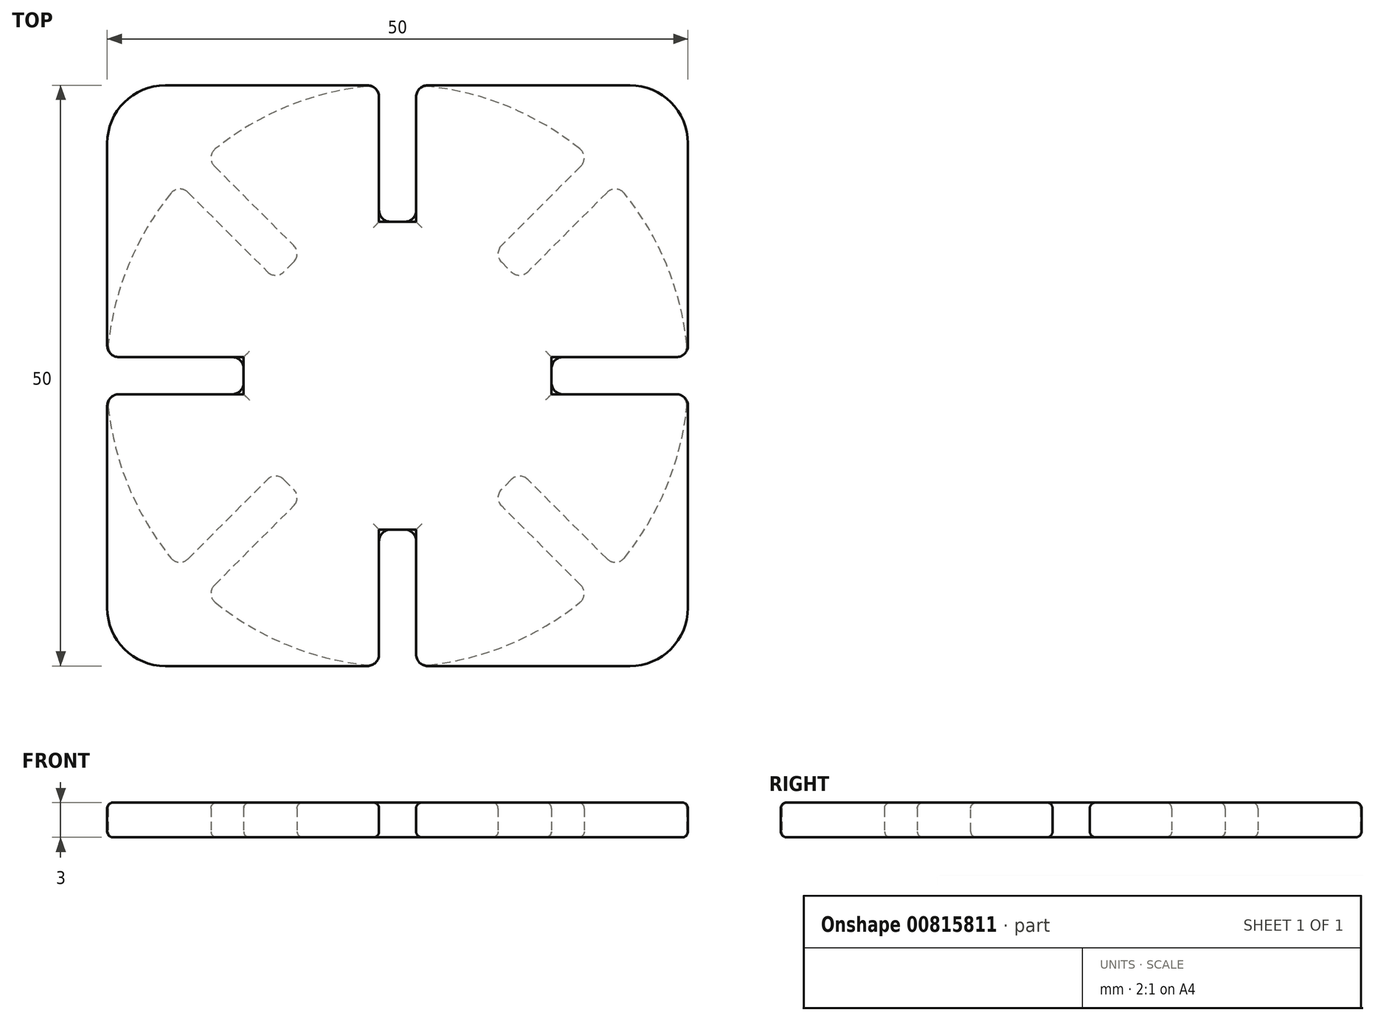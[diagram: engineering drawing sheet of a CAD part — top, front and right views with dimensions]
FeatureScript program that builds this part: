
annotation { "Feature Type Name" : "Feature", "Feature Type Description" : "" }
export const myFeature = defineFeature(function(context is Context, id is Id, definition is map)
    precondition{}
    {
        {
            assignVariable(context, id + "F0", {"name" : "thickness", "anyValue" : 3 * mm});
        }
        {
            var Q0;
            Q0=qCreatedBy(makeId("Top.planeOp"),FACE);
            var sketch = newSketch(context, id + "F1", { "sketchPlane" : qUnion([Q0])});
            skLineSegment(sketch, "E0.bottom", {"start": v(25, -25) * mm, "end": v(-25, -25) * mm});
            skLineSegment(sketch, "E0.top", {"start": v(25, 25) * mm, "end": v(-25, 25) * mm});
            skLineSegment(sketch, "E0.left", {"start": v(25, -25) * mm, "end": v(25, 25) * mm});
            skLineSegment(sketch, "E0.right", {"start": v(-25, -25) * mm, "end": v(-25, 25) * mm});
            skPoint(sketch, "E0.middle", {"position": v(0, 0) * mm});
            skLineSegment(sketch, "E1.bottom", {"start": v(25, 1.6) * mm, "end": v(13.25, 1.6) * mm});
            skLineSegment(sketch, "E1.top", {"start": v(25, -1.6) * mm, "end": v(13.25, -1.6) * mm});
            skLineSegment(sketch, "E1.left", {"start": v(25, 1.6) * mm, "end": v(25, -1.6) * mm});
            skLineSegment(sketch, "E1.right", {"start": v(13.25, 1.6) * mm, "end": v(13.25, -1.6) * mm});
            skLineSegment(sketch, "E2.bottom", {"start": v(-25, 1.6) * mm, "end": v(-13.25, 1.6) * mm});
            skLineSegment(sketch, "E2.top", {"start": v(-25, -1.6) * mm, "end": v(-13.25, -1.6) * mm});
            skLineSegment(sketch, "E2.left", {"start": v(-25, 1.6) * mm, "end": v(-25, -1.6) * mm});
            skLineSegment(sketch, "E2.right", {"start": v(-13.25, 1.6) * mm, "end": v(-13.25, -1.6) * mm});
            skLineSegment(sketch, "E3.bottom", {"start": v(-1.6, 25) * mm, "end": v(1.6, 25) * mm});
            skLineSegment(sketch, "E3.top", {"start": v(-1.6, 13.25) * mm, "end": v(1.6, 13.25) * mm});
            skLineSegment(sketch, "E3.left", {"start": v(-1.6, 25) * mm, "end": v(-1.6, 13.25) * mm});
            skLineSegment(sketch, "E3.right", {"start": v(1.6, 25) * mm, "end": v(1.6, 13.25) * mm});
            skLineSegment(sketch, "E4.bottom", {"start": v(-1.6, -25) * mm, "end": v(1.6, -25) * mm});
            skLineSegment(sketch, "E4.top", {"start": v(-1.6, -13.25) * mm, "end": v(1.6, -13.25) * mm});
            skLineSegment(sketch, "E4.left", {"start": v(-1.6, -25) * mm, "end": v(-1.6, -13.25) * mm});
            skLineSegment(sketch, "E4.right", {"start": v(1.6, -25) * mm, "end": v(1.6, -13.25) * mm});
            skSolve(sketch);
        }
        {
            var Q0;
            {var subQ1=sQuery(id+"F1.wireOp",EDGE,"E1.bottom");Q0=makeQuery(id+"F1.imprint","IMPRINT",FACE,{"disambiguationData":[TD([[makeQuery(id+"F1.imprint","IMPRINT",EDGE,{"derivedFrom":subQ1}),-1.0]])]});}
            extrude(context, id + "F2", {"entities" : qUnion([Q0]), "depth" : getVariable(context, 'thickness'), "offsetDistance" : 25 * mm});
        }
        {
            var Q0;
            Q0=makeQuery(id+"F2.opExtrude","SWEPT_EDGE",EDGE,{"disambiguationData":[OSD([sQuery(id+"F1.wireOp",EDGE,"E0.bottom"),sQuery(id+"F1.wireOp",EDGE,"E0.left")])]});
            var Q1;
            Q1=makeQuery(id+"F2.opExtrude","SWEPT_EDGE",EDGE,{"disambiguationData":[OSD([sQuery(id+"F1.wireOp",EDGE,"E0.bottom"),sQuery(id+"F1.wireOp",EDGE,"E0.right")])]});
            var Q2;
            Q2=makeQuery(id+"F2.opExtrude","SWEPT_EDGE",EDGE,{"disambiguationData":[OSD([sQuery(id+"F1.wireOp",EDGE,"E0.top"),sQuery(id+"F1.wireOp",EDGE,"E0.left")])]});
            var Q3;
            Q3=makeQuery(id+"F2.opExtrude","SWEPT_EDGE",EDGE,{"disambiguationData":[OSD([sQuery(id+"F1.wireOp",EDGE,"E0.top"),sQuery(id+"F1.wireOp",EDGE,"E0.right")])]});
            fillet(context, id + "F3", {"entities" : qUnion([Q0, Q1, Q2, Q3]), "radius" : 5 * mm, "tangentPropagation" : true, "allowEdgeOverflow" : false});
        }
        {
            var Q0;
            Q0=makeQuery(id+"F2.opExtrude","SWEPT_EDGE",EDGE,{"disambiguationData":[OSD([sQuery(id+"F1.wireOp",EDGE,"E0.bottom"),sQuery(id+"F1.wireOp",EDGE,"E4.bottom"),sQuery(id+"F1.wireOp",EDGE,"E4.left")])]});
            var Q1;
            Q1=makeQuery(id+"F2.opExtrude","SWEPT_EDGE",EDGE,{"disambiguationData":[OSD([sQuery(id+"F1.wireOp",EDGE,"E0.bottom"),sQuery(id+"F1.wireOp",EDGE,"E4.bottom"),sQuery(id+"F1.wireOp",EDGE,"E4.right")])]});
            var Q2;
            Q2=makeQuery(id+"F2.opExtrude","SWEPT_EDGE",EDGE,{"disambiguationData":[OSD([sQuery(id+"F1.wireOp",EDGE,"E0.left"),sQuery(id+"F1.wireOp",EDGE,"E1.top"),sQuery(id+"F1.wireOp",EDGE,"E1.left")])]});
            var Q3;
            Q3=makeQuery(id+"F2.opExtrude","SWEPT_EDGE",EDGE,{"disambiguationData":[OSD([sQuery(id+"F1.wireOp",EDGE,"E0.left"),sQuery(id+"F1.wireOp",EDGE,"E1.bottom"),sQuery(id+"F1.wireOp",EDGE,"E1.left")])]});
            var Q4;
            Q4=makeQuery(id+"F2.opExtrude","SWEPT_EDGE",EDGE,{"disambiguationData":[OSD([sQuery(id+"F1.wireOp",EDGE,"E0.right"),sQuery(id+"F1.wireOp",EDGE,"E2.bottom"),sQuery(id+"F1.wireOp",EDGE,"E2.left")])]});
            var Q5;
            Q5=makeQuery(id+"F2.opExtrude","SWEPT_EDGE",EDGE,{"disambiguationData":[OSD([sQuery(id+"F1.wireOp",EDGE,"E0.top"),sQuery(id+"F1.wireOp",EDGE,"E3.bottom"),sQuery(id+"F1.wireOp",EDGE,"E3.left")])]});
            var Q6;
            Q6=makeQuery(id+"F2.opExtrude","SWEPT_EDGE",EDGE,{"disambiguationData":[OSD([sQuery(id+"F1.wireOp",EDGE,"E0.top"),sQuery(id+"F1.wireOp",EDGE,"E3.bottom"),sQuery(id+"F1.wireOp",EDGE,"E3.right")])]});
            var Q7;
            Q7=makeQuery(id+"F2.opExtrude","SWEPT_EDGE",EDGE,{"disambiguationData":[OSD([sQuery(id+"F1.wireOp",EDGE,"E0.right"),sQuery(id+"F1.wireOp",EDGE,"E2.top"),sQuery(id+"F1.wireOp",EDGE,"E2.left")])]});
            fillet(context, id + "F4", {"entities" : qUnion([Q0, Q1, Q2, Q3, Q4, Q5, Q6, Q7]), "radius" : 1 * mm, "tangentPropagation" : true, "allowEdgeOverflow" : false});
        }
        {
            var Q0;
            Q0=makeQuery(id+"F2.opExtrude","CAP_FACE",FACE,{"disambiguationData":[OSD([sQuery(id+"F1.wireOp",EDGE,"E0.bottom"),sQuery(id+"F1.wireOp",EDGE,"E0.top"),sQuery(id+"F1.wireOp",EDGE,"E0.left"),sQuery(id+"F1.wireOp",EDGE,"E0.right"),sQuery(id+"F1.wireOp",EDGE,"E1.bottom"),sQuery(id+"F1.wireOp",EDGE,"E1.top"),sQuery(id+"F1.wireOp",EDGE,"E1.right"),sQuery(id+"F1.wireOp",EDGE,"E2.bottom"),sQuery(id+"F1.wireOp",EDGE,"E2.top"),sQuery(id+"F1.wireOp",EDGE,"E2.right"),sQuery(id+"F1.wireOp",EDGE,"E3.top"),sQuery(id+"F1.wireOp",EDGE,"E3.left"),sQuery(id+"F1.wireOp",EDGE,"E3.right"),sQuery(id+"F1.wireOp",EDGE,"E4.top"),sQuery(id+"F1.wireOp",EDGE,"E4.left"),sQuery(id+"F1.wireOp",EDGE,"E4.right")])],"isStart":true});
            var Q1;
            Q1=makeQuery(id+"F2.opExtrude","CAP_FACE",FACE,{"disambiguationData":[OSD([sQuery(id+"F1.wireOp",EDGE,"E0.bottom"),sQuery(id+"F1.wireOp",EDGE,"E0.top"),sQuery(id+"F1.wireOp",EDGE,"E0.left"),sQuery(id+"F1.wireOp",EDGE,"E0.right"),sQuery(id+"F1.wireOp",EDGE,"E1.bottom"),sQuery(id+"F1.wireOp",EDGE,"E1.top"),sQuery(id+"F1.wireOp",EDGE,"E1.right"),sQuery(id+"F1.wireOp",EDGE,"E2.bottom"),sQuery(id+"F1.wireOp",EDGE,"E2.top"),sQuery(id+"F1.wireOp",EDGE,"E2.right"),sQuery(id+"F1.wireOp",EDGE,"E3.top"),sQuery(id+"F1.wireOp",EDGE,"E3.left"),sQuery(id+"F1.wireOp",EDGE,"E3.right"),sQuery(id+"F1.wireOp",EDGE,"E4.top"),sQuery(id+"F1.wireOp",EDGE,"E4.left"),sQuery(id+"F1.wireOp",EDGE,"E4.right")])],"isStart":false});
            fillet(context, id + "F5", {"entities" : qUnion([Q0, Q1]), "radius" : .5 * mm, "tangentPropagation" : true, "allowEdgeOverflow" : false});
        }
        {
            var Q0;
            Q0=qCreatedBy(makeId("Top.planeOp"),FACE);
            var sketch = newSketch(context, id + "F6", { "sketchPlane" : qUnion([Q0])});
            skLineSegment(sketch, "E5.0", {"start": v(25, 1.6) * mm, "end": v(13.25, 1.6) * mm});
            skLineSegment(sketch, "E5.1", {"start": v(-25, -1.6) * mm, "end": v(-13.25, -1.6) * mm});
            skLineSegment(sketch, "E5.2", {"start": v(-1.6, 13.25) * mm, "end": v(1.6, 13.25) * mm});
            skLineSegment(sketch, "E5.3", {"start": v(-25, 1.6) * mm, "end": v(-13.25, 1.6) * mm});
            skLineSegment(sketch, "E5.4", {"start": v(-13.25, 1.6) * mm, "end": v(-13.25, -1.6) * mm});
            skLineSegment(sketch, "E5.8", {"start": v(-1.6, -25) * mm, "end": v(-1.6, -13.25) * mm});
            skLineSegment(sketch, "E5.9", {"start": v(-1.6, -13.25) * mm, "end": v(1.6, -13.25) * mm});
            skLineSegment(sketch, "E5.10", {"start": v(-1.6, 25) * mm, "end": v(-1.6, 13.25) * mm});
            skLineSegment(sketch, "E5.12", {"start": v(25, -1.6) * mm, "end": v(13.25, -1.6) * mm});
            skLineSegment(sketch, "E5.15", {"start": v(1.6, -25) * mm, "end": v(1.6, -13.25) * mm});
            skLineSegment(sketch, "E5.16", {"start": v(13.25, 1.6) * mm, "end": v(13.25, -1.6) * mm});
            skLineSegment(sketch, "E5.17", {"start": v(1.6, 25) * mm, "end": v(1.6, 13.25) * mm});
            skPoint(sketch, "E5.6.end.orphan", {"position": v(25, 1.6) * mm});
            skPoint(sketch, "E5.6.start.orphan", {"position": v(25, -1.6) * mm});
            skPoint(sketch, "E5.14.end.orphan", {"position": v(1.6, -25) * mm});
            skPoint(sketch, "E5.14.start.orphan", {"position": v(-1.6, -25) * mm});
            skPoint(sketch, "E5.7.end.orphan", {"position": v(1.6, 25) * mm});
            skPoint(sketch, "E5.7.start.orphan", {"position": v(-1.6, 25) * mm});
            skPoint(sketch, "E5.5.end.orphan", {"position": v(-25, -1.6) * mm});
            skPoint(sketch, "E5.5.start.orphan", {"position": v(-25, 1.6) * mm});
            skPoint(sketch, "E6.1.0", {"position": v(-18.8, 16.55) * mm});
            skLineSegment(sketch, "E6.1.1", {"start": v(16.55, -18.8) * mm, "end": v(8.24, -10.5) * mm});
            skLineSegment(sketch, "E6.1.2", {"start": v(-16.55, 18.8) * mm, "end": v(-8.24, 10.5) * mm});
            skPoint(sketch, "E6.1.3", {"position": v(-18.8, -16.55) * mm});
            skPoint(sketch, "E6.1.4", {"position": v(-16.55, -18.8) * mm});
            skLineSegment(sketch, "E6.1.5", {"start": v(18.8, -16.55) * mm, "end": v(10.5, -8.24) * mm});
            skPoint(sketch, "E6.1.6", {"position": v(16.55, 18.8) * mm});
            skLineSegment(sketch, "E6.1.7", {"start": v(18.8, 16.55) * mm, "end": v(10.5, 8.24) * mm});
            skPoint(sketch, "E6.1.8", {"position": v(18.8, 16.55) * mm});
            skPoint(sketch, "E6.1.9", {"position": v(18.8, -16.55) * mm});
            skLineSegment(sketch, "E6.1.10", {"start": v(-16.55, -18.8) * mm, "end": v(-8.24, -10.5) * mm});
            skPoint(sketch, "E6.1.11", {"position": v(16.55, -18.8) * mm});
            skLineSegment(sketch, "E6.1.12", {"start": v(-18.8, 16.55) * mm, "end": v(-10.5, 8.24) * mm});
            skLineSegment(sketch, "E6.1.13", {"start": v(-18.8, -16.55) * mm, "end": v(-10.5, -8.24) * mm});
            skLineSegment(sketch, "E6.1.14", {"start": v(16.55, 18.8) * mm, "end": v(8.24, 10.5) * mm});
            skPoint(sketch, "E6.1.15", {"position": v(-16.55, 18.8) * mm});
            skLineSegment(sketch, "E6.1.16", {"start": v(10.5, -8.24) * mm, "end": v(8.24, -10.5) * mm});
            skLineSegment(sketch, "E6.1.17", {"start": v(8.24, 10.5) * mm, "end": v(10.5, 8.24) * mm});
            skLineSegment(sketch, "E6.1.18", {"start": v(-8.24, 10.5) * mm, "end": v(-10.5, 8.24) * mm});
            skLineSegment(sketch, "E6.1.19", {"start": v(-10.5, -8.24) * mm, "end": v(-8.24, -10.5) * mm});
            skPoint(sketch, "E6.center", {"position": v(0, 0) * mm});
            skLineSegment(sketch, "E6.anchor1", {"start": v(0, 0) * mm, "end": v(-1.6, -13.25) * mm, "construction": true});
            skLineSegment(sketch, "E6.anchor2", {"start": v(0, 0) * mm, "end": v(-10.5, -8.24) * mm, "construction": true});
            skArc(sketch, "E7", {"start": v(-1.6, 25) * mm, "mid": v(-9.59, 23.14) * mm, "end": v(-16.55, 18.8) * mm});
            skArc(sketch, "E8.trimOffspring", {"start": v(-18.8, 16.55) * mm, "mid": v(-23.14, 9.59) * mm, "end": v(-25, 1.6) * mm});
            skArc(sketch, "E9.trimOffspring", {"start": v(-25, -1.6) * mm, "mid": v(-23.14, -9.59) * mm, "end": v(-18.8, -16.55) * mm});
            skArc(sketch, "E10.trimOffspring", {"start": v(-16.55, -18.8) * mm, "mid": v(-9.59, -23.14) * mm, "end": v(-1.6, -25) * mm});
            skArc(sketch, "E11.trimOffspring", {"start": v(1.6, -25) * mm, "mid": v(9.59, -23.14) * mm, "end": v(16.55, -18.8) * mm});
            skArc(sketch, "E12.trimOffspring", {"start": v(18.8, -16.55) * mm, "mid": v(23.14, -9.59) * mm, "end": v(25, -1.6) * mm});
            skArc(sketch, "E13.trimOffspring", {"start": v(25, 1.6) * mm, "mid": v(23.14, 9.59) * mm, "end": v(18.8, 16.55) * mm});
            skArc(sketch, "E14.trimOffspring", {"start": v(16.55, 18.8) * mm, "mid": v(9.59, 23.14) * mm, "end": v(1.6, 25) * mm});
            skSolve(sketch);
        }
        {
            var Q0;
            Q0=makeQuery(id+"F6.imprint","IMPRINT",FACE,{"disambiguationData":[TD([[makeQuery(id+"F6.imprint","IMPRINT",EDGE,{"derivedFrom":sQuery(id+"F6.wireOp",EDGE,"E5.0")}),-1.0]])]});
            extrude(context, id + "F7", {"entities" : qUnion([Q0]), "depth" : getVariable(context, 'thickness'), "offsetDistance" : 25 * mm});
        }
        {
            var Q0;
            Q0=makeQuery(id+"F7.opExtrude","SWEPT_EDGE",EDGE,{"disambiguationData":[OSD([sQuery(id+"F6.wireOp",EDGE,"E6.1.2"),sQuery(id+"F6.wireOp",EDGE,"E6.1.18")])]});
            var Q1;
            Q1=makeQuery(id+"F7.opExtrude","SWEPT_EDGE",EDGE,{"disambiguationData":[OSD([sQuery(id+"F6.wireOp",EDGE,"E5.2"),sQuery(id+"F6.wireOp",EDGE,"E5.17")])]});
            var Q2;
            Q2=makeQuery(id+"F7.opExtrude","SWEPT_EDGE",EDGE,{"disambiguationData":[OSD([sQuery(id+"F6.wireOp",EDGE,"E6.1.10"),sQuery(id+"F6.wireOp",EDGE,"E6.1.19")])]});
            var Q3;
            Q3=makeQuery(id+"F7.opExtrude","SWEPT_EDGE",EDGE,{"disambiguationData":[OSD([sQuery(id+"F6.wireOp",EDGE,"E5.1"),sQuery(id+"F6.wireOp",EDGE,"E5.4")])]});
            var Q4;
            Q4=makeQuery(id+"F7.opExtrude","SWEPT_EDGE",EDGE,{"disambiguationData":[OSD([sQuery(id+"F6.wireOp",EDGE,"E6.1.2"),sQuery(id+"F6.wireOp",EDGE,"E7")])]});
            var Q5;
            Q5=makeQuery(id+"F7.opExtrude","SWEPT_EDGE",EDGE,{"disambiguationData":[OSD([sQuery(id+"F6.wireOp",EDGE,"E6.1.12"),sQuery(id+"F6.wireOp",EDGE,"E8.trimOffspring")])]});
            var Q6;
            Q6=makeQuery(id+"F7.opExtrude","SWEPT_EDGE",EDGE,{"disambiguationData":[OSD([sQuery(id+"F6.wireOp",EDGE,"E5.3"),sQuery(id+"F6.wireOp",EDGE,"E8.trimOffspring")])]});
            var Q7;
            Q7=makeQuery(id+"F7.opExtrude","SWEPT_EDGE",EDGE,{"disambiguationData":[OSD([sQuery(id+"F6.wireOp",EDGE,"E5.1"),sQuery(id+"F6.wireOp",EDGE,"E9.trimOffspring")])]});
            var Q8;
            Q8=makeQuery(id+"F7.opExtrude","SWEPT_EDGE",EDGE,{"disambiguationData":[OSD([sQuery(id+"F6.wireOp",EDGE,"E6.1.13"),sQuery(id+"F6.wireOp",EDGE,"E9.trimOffspring")])]});
            var Q9;
            Q9=makeQuery(id+"F7.opExtrude","SWEPT_EDGE",EDGE,{"disambiguationData":[OSD([sQuery(id+"F6.wireOp",EDGE,"E6.1.10"),sQuery(id+"F6.wireOp",EDGE,"E10.trimOffspring")])]});
            var Q10;
            Q10=makeQuery(id+"F7.opExtrude","SWEPT_EDGE",EDGE,{"disambiguationData":[OSD([sQuery(id+"F6.wireOp",EDGE,"E6.1.5"),sQuery(id+"F6.wireOp",EDGE,"E12.trimOffspring")])]});
            var Q11;
            Q11=makeQuery(id+"F7.opExtrude","SWEPT_EDGE",EDGE,{"disambiguationData":[OSD([sQuery(id+"F6.wireOp",EDGE,"E5.12"),sQuery(id+"F6.wireOp",EDGE,"E12.trimOffspring")])]});
            var Q12;
            Q12=makeQuery(id+"F7.opExtrude","SWEPT_EDGE",EDGE,{"disambiguationData":[OSD([sQuery(id+"F6.wireOp",EDGE,"E5.10"),sQuery(id+"F6.wireOp",EDGE,"E7")])]});
            var Q13;
            Q13=makeQuery(id+"F7.opExtrude","SWEPT_EDGE",EDGE,{"disambiguationData":[OSD([sQuery(id+"F6.wireOp",EDGE,"E5.17"),sQuery(id+"F6.wireOp",EDGE,"E14.trimOffspring")])]});
            var Q14;
            Q14=makeQuery(id+"F7.opExtrude","SWEPT_EDGE",EDGE,{"disambiguationData":[OSD([sQuery(id+"F6.wireOp",EDGE,"E6.1.7"),sQuery(id+"F6.wireOp",EDGE,"E13.trimOffspring")])]});
            var Q15;
            Q15=makeQuery(id+"F7.opExtrude","SWEPT_EDGE",EDGE,{"disambiguationData":[OSD([sQuery(id+"F6.wireOp",EDGE,"E6.1.14"),sQuery(id+"F6.wireOp",EDGE,"E14.trimOffspring")])]});
            var Q16;
            Q16=makeQuery(id+"F7.opExtrude","SWEPT_EDGE",EDGE,{"disambiguationData":[OSD([sQuery(id+"F6.wireOp",EDGE,"E6.1.14"),sQuery(id+"F6.wireOp",EDGE,"E6.1.17")])]});
            var Q17;
            Q17=makeQuery(id+"F7.opExtrude","SWEPT_EDGE",EDGE,{"disambiguationData":[OSD([sQuery(id+"F6.wireOp",EDGE,"E5.2"),sQuery(id+"F6.wireOp",EDGE,"E5.10")])]});
            var Q18;
            Q18=makeQuery(id+"F7.opExtrude","SWEPT_EDGE",EDGE,{"disambiguationData":[OSD([sQuery(id+"F6.wireOp",EDGE,"E5.12"),sQuery(id+"F6.wireOp",EDGE,"E5.16")])]});
            var Q19;
            Q19=makeQuery(id+"F7.opExtrude","SWEPT_EDGE",EDGE,{"disambiguationData":[OSD([sQuery(id+"F6.wireOp",EDGE,"E6.1.1"),sQuery(id+"F6.wireOp",EDGE,"E6.1.16")])]});
            var Q20;
            Q20=makeQuery(id+"F7.opExtrude","SWEPT_EDGE",EDGE,{"disambiguationData":[OSD([sQuery(id+"F6.wireOp",EDGE,"E6.1.1"),sQuery(id+"F6.wireOp",EDGE,"E11.trimOffspring")])]});
            var Q21;
            Q21=makeQuery(id+"F7.opExtrude","SWEPT_EDGE",EDGE,{"disambiguationData":[OSD([sQuery(id+"F6.wireOp",EDGE,"E5.0"),sQuery(id+"F6.wireOp",EDGE,"E13.trimOffspring")])]});
            var Q22;
            Q22=makeQuery(id+"F7.opExtrude","SWEPT_EDGE",EDGE,{"disambiguationData":[OSD([sQuery(id+"F6.wireOp",EDGE,"E5.8"),sQuery(id+"F6.wireOp",EDGE,"E10.trimOffspring")])]});
            var Q23;
            Q23=makeQuery(id+"F7.opExtrude","SWEPT_EDGE",EDGE,{"disambiguationData":[OSD([sQuery(id+"F6.wireOp",EDGE,"E5.8"),sQuery(id+"F6.wireOp",EDGE,"E5.9")])]});
            var Q24;
            Q24=makeQuery(id+"F7.opExtrude","SWEPT_EDGE",EDGE,{"disambiguationData":[OSD([sQuery(id+"F6.wireOp",EDGE,"E5.15"),sQuery(id+"F6.wireOp",EDGE,"E11.trimOffspring")])]});
            var Q25;
            Q25=makeQuery(id+"F7.opExtrude","SWEPT_EDGE",EDGE,{"disambiguationData":[OSD([sQuery(id+"F6.wireOp",EDGE,"E6.1.13"),sQuery(id+"F6.wireOp",EDGE,"E6.1.19")])]});
            var Q26;
            Q26=makeQuery(id+"F7.opExtrude","SWEPT_EDGE",EDGE,{"disambiguationData":[OSD([sQuery(id+"F6.wireOp",EDGE,"E5.3"),sQuery(id+"F6.wireOp",EDGE,"E5.4")])]});
            var Q27;
            Q27=makeQuery(id+"F7.opExtrude","SWEPT_EDGE",EDGE,{"disambiguationData":[OSD([sQuery(id+"F6.wireOp",EDGE,"E6.1.5"),sQuery(id+"F6.wireOp",EDGE,"E6.1.16")])]});
            var Q28;
            Q28=makeQuery(id+"F7.opExtrude","SWEPT_EDGE",EDGE,{"disambiguationData":[OSD([sQuery(id+"F6.wireOp",EDGE,"E6.1.12"),sQuery(id+"F6.wireOp",EDGE,"E6.1.18")])]});
            var Q29;
            Q29=makeQuery(id+"F7.opExtrude","SWEPT_EDGE",EDGE,{"disambiguationData":[OSD([sQuery(id+"F6.wireOp",EDGE,"E6.1.7"),sQuery(id+"F6.wireOp",EDGE,"E6.1.17")])]});
            var Q30;
            Q30=makeQuery(id+"F7.opExtrude","SWEPT_EDGE",EDGE,{"disambiguationData":[OSD([sQuery(id+"F6.wireOp",EDGE,"E5.0"),sQuery(id+"F6.wireOp",EDGE,"E5.16")])]});
            var Q31;
            Q31=makeQuery(id+"F7.opExtrude","SWEPT_EDGE",EDGE,{"disambiguationData":[OSD([sQuery(id+"F6.wireOp",EDGE,"E5.9"),sQuery(id+"F6.wireOp",EDGE,"E5.15")])]});
            fillet(context, id + "F8", {"entities" : qUnion([Q0, Q1, Q2, Q3, Q4, Q5, Q6, Q7, Q8, Q9, Q10, Q11, Q12, Q13, Q14, Q15, Q16, Q17, Q18, Q19, Q20, Q21, Q22, Q23, Q24, Q25, Q26, Q27, Q28, Q29, Q30, Q31]), "radius" : 1 * mm, "tangentPropagation" : true, "allowEdgeOverflow" : false});
        }
        {
            var Q0;
            Q0=makeQuery(id+"F7.opExtrude","CAP_FACE",FACE,{"disambiguationData":[OSD([sQuery(id+"F6.wireOp",EDGE,"o8u2ld8t-ahjA-RV4m-6lsj-Seaqtk0HvvEa"),sQuery(id+"F6.wireOp",EDGE,"686bb1c4-31b7-4a5b-a7db-e06899689aa9.0.1"),sQuery(id+"F6.wireOp",EDGE,"686bb1c4-31b7-4a5b-a7db-e06899689aa9.0.2"),sQuery(id+"F6.wireOp",EDGE,"686bb1c4-31b7-4a5b-a7db-e06899689aa9.0.3"),sQuery(id+"F6.wireOp",EDGE,"eeb81bc5-d00c-4a1c-84e7-1b76d88a8212.0.0"),sQuery(id+"F6.wireOp",EDGE,"eeb81bc5-d00c-4a1c-84e7-1b76d88a8212.0.2"),sQuery(id+"F6.wireOp",EDGE,"eeb81bc5-d00c-4a1c-84e7-1b76d88a8212.0.3"),sQuery(id+"F6.wireOp",EDGE,"a30ab006-903c-44b7-bced-bb320873270e.0.0"),sQuery(id+"F6.wireOp",EDGE,"a30ab006-903c-44b7-bced-bb320873270e.0.2"),sQuery(id+"F6.wireOp",EDGE,"a30ab006-903c-44b7-bced-bb320873270e.0.3"),sQuery(id+"F6.wireOp",EDGE,"b52b4c88-fd28-43ae-979c-353055610e24.0.1"),sQuery(id+"F6.wireOp",EDGE,"b52b4c88-fd28-43ae-979c-353055610e24.0.2"),sQuery(id+"F6.wireOp",EDGE,"b52b4c88-fd28-43ae-979c-353055610e24.0.3"),sQuery(id+"F6.wireOp",EDGE,"849ee18c-69b4-4aa5-a0a1-a98ea034f52a.trimOffspring"),sQuery(id+"F6.wireOp",EDGE,"246bdb21-8b35-4ed6-893b-f867f6443165.trimOffspring"),sQuery(id+"F6.wireOp",EDGE,"e6d6c3ad-90c8-4466-9c71-280e11051eb6.trimOffspring")])],"isStart":false});
            var Q1;
            Q1=makeQuery(id+"F7.opExtrude","CAP_FACE",FACE,{"disambiguationData":[OSD([sQuery(id+"F6.wireOp",EDGE,"o8u2ld8t-ahjA-RV4m-6lsj-Seaqtk0HvvEa"),sQuery(id+"F6.wireOp",EDGE,"686bb1c4-31b7-4a5b-a7db-e06899689aa9.0.1"),sQuery(id+"F6.wireOp",EDGE,"686bb1c4-31b7-4a5b-a7db-e06899689aa9.0.2"),sQuery(id+"F6.wireOp",EDGE,"686bb1c4-31b7-4a5b-a7db-e06899689aa9.0.3"),sQuery(id+"F6.wireOp",EDGE,"eeb81bc5-d00c-4a1c-84e7-1b76d88a8212.0.0"),sQuery(id+"F6.wireOp",EDGE,"eeb81bc5-d00c-4a1c-84e7-1b76d88a8212.0.2"),sQuery(id+"F6.wireOp",EDGE,"eeb81bc5-d00c-4a1c-84e7-1b76d88a8212.0.3"),sQuery(id+"F6.wireOp",EDGE,"a30ab006-903c-44b7-bced-bb320873270e.0.0"),sQuery(id+"F6.wireOp",EDGE,"a30ab006-903c-44b7-bced-bb320873270e.0.2"),sQuery(id+"F6.wireOp",EDGE,"a30ab006-903c-44b7-bced-bb320873270e.0.3"),sQuery(id+"F6.wireOp",EDGE,"b52b4c88-fd28-43ae-979c-353055610e24.0.1"),sQuery(id+"F6.wireOp",EDGE,"b52b4c88-fd28-43ae-979c-353055610e24.0.2"),sQuery(id+"F6.wireOp",EDGE,"b52b4c88-fd28-43ae-979c-353055610e24.0.3"),sQuery(id+"F6.wireOp",EDGE,"849ee18c-69b4-4aa5-a0a1-a98ea034f52a.trimOffspring"),sQuery(id+"F6.wireOp",EDGE,"246bdb21-8b35-4ed6-893b-f867f6443165.trimOffspring"),sQuery(id+"F6.wireOp",EDGE,"e6d6c3ad-90c8-4466-9c71-280e11051eb6.trimOffspring")])],"isStart":true});
            var Q2;
            Q2=makeQuery(id+"F7.opExtrude","CAP_FACE",FACE,{"disambiguationData":[OSD([sQuery(id+"F6.wireOp",EDGE,"818c942b-1b27-44ba-9c31-6e242bf95702.0.1"),sQuery(id+"F6.wireOp",EDGE,"818c942b-1b27-44ba-9c31-6e242bf95702.0.2"),sQuery(id+"F6.wireOp",EDGE,"818c942b-1b27-44ba-9c31-6e242bf95702.0.3"),sQuery(id+"F6.wireOp",EDGE,"c0eba70a-3e61-4e7f-990b-f91f08fd2a50.0.0"),sQuery(id+"F6.wireOp",EDGE,"c0eba70a-3e61-4e7f-990b-f91f08fd2a50.0.2"),sQuery(id+"F6.wireOp",EDGE,"c0eba70a-3e61-4e7f-990b-f91f08fd2a50.0.3"),sQuery(id+"F6.wireOp",EDGE,"efac9003-0ea8-4251-97d7-c1478ef51c29.0.1"),sQuery(id+"F6.wireOp",EDGE,"efac9003-0ea8-4251-97d7-c1478ef51c29.0.2"),sQuery(id+"F6.wireOp",EDGE,"efac9003-0ea8-4251-97d7-c1478ef51c29.0.3"),sQuery(id+"F6.wireOp",EDGE,"89777391-df2a-4d0b-bbf8-c0feeb0d1ef7.0.0"),sQuery(id+"F6.wireOp",EDGE,"89777391-df2a-4d0b-bbf8-c0feeb0d1ef7.0.2"),sQuery(id+"F6.wireOp",EDGE,"89777391-df2a-4d0b-bbf8-c0feeb0d1ef7.0.3"),sQuery(id+"F6.wireOp",EDGE,"5c4a4382-07f6-4214-aac6-78221b16e3d7.0.1"),sQuery(id+"F6.wireOp",EDGE,"5c4a4382-07f6-4214-aac6-78221b16e3d7.0.2"),sQuery(id+"F6.wireOp",EDGE,"5c4a4382-07f6-4214-aac6-78221b16e3d7.0.3"),sQuery(id+"F6.wireOp",EDGE,"f066974f-1994-491f-a93d-417e52911a5a.0.0"),sQuery(id+"F6.wireOp",EDGE,"f066974f-1994-491f-a93d-417e52911a5a.0.2"),sQuery(id+"F6.wireOp",EDGE,"f066974f-1994-491f-a93d-417e52911a5a.0.3"),sQuery(id+"F6.wireOp",EDGE,"95247560-69bb-48ff-a0da-1bb4b4d30057.0.1"),sQuery(id+"F6.wireOp",EDGE,"95247560-69bb-48ff-a0da-1bb4b4d30057.0.2"),sQuery(id+"F6.wireOp",EDGE,"95247560-69bb-48ff-a0da-1bb4b4d30057.0.3"),sQuery(id+"F6.wireOp",EDGE,"1d799f85-7818-430d-bbf1-0f564a028ddc.0.0"),sQuery(id+"F6.wireOp",EDGE,"1d799f85-7818-430d-bbf1-0f564a028ddc.0.2"),sQuery(id+"F6.wireOp",EDGE,"1d799f85-7818-430d-bbf1-0f564a028ddc.0.3"),sQuery(id+"F6.wireOp",EDGE,"6aa83139-d0d5-4dfc-9373-fda511bd29d7.trimOffspring"),sQuery(id+"F6.wireOp",EDGE,"1408c1dd-e7a2-410c-9066-205276191e3a.trimOffspring"),sQuery(id+"F6.wireOp",EDGE,"e31db4b1-2812-45a9-86ec-e541b6eb03b3.trimOffspring"),sQuery(id+"F6.wireOp",EDGE,"726fdc42-c52d-414d-8529-3d57c62d2646.trimOffspring"),sQuery(id+"F6.wireOp",EDGE,"85645508-a54a-4e30-b284-8fd3e0c44a2d.trimOffspring"),sQuery(id+"F6.wireOp",EDGE,"f6c9b0fd-1728-47da-b042-307b3b696b93.trimOffspring"),sQuery(id+"F6.wireOp",EDGE,"70f4a275-a1fe-4adc-966b-bca2063eecaf.trimOffspring"),sQuery(id+"F6.wireOp",EDGE,"3e7ab608-056d-4084-b8cf-19f53ae0a1b8.trimOffspring")])],"isStart":false});
            var Q3;
            Q3=makeQuery(id+"F7.opExtrude","CAP_FACE",FACE,{"disambiguationData":[OSD([sQuery(id+"F6.wireOp",EDGE,"818c942b-1b27-44ba-9c31-6e242bf95702.0.1"),sQuery(id+"F6.wireOp",EDGE,"818c942b-1b27-44ba-9c31-6e242bf95702.0.2"),sQuery(id+"F6.wireOp",EDGE,"818c942b-1b27-44ba-9c31-6e242bf95702.0.3"),sQuery(id+"F6.wireOp",EDGE,"c0eba70a-3e61-4e7f-990b-f91f08fd2a50.0.0"),sQuery(id+"F6.wireOp",EDGE,"c0eba70a-3e61-4e7f-990b-f91f08fd2a50.0.2"),sQuery(id+"F6.wireOp",EDGE,"c0eba70a-3e61-4e7f-990b-f91f08fd2a50.0.3"),sQuery(id+"F6.wireOp",EDGE,"efac9003-0ea8-4251-97d7-c1478ef51c29.0.1"),sQuery(id+"F6.wireOp",EDGE,"efac9003-0ea8-4251-97d7-c1478ef51c29.0.2"),sQuery(id+"F6.wireOp",EDGE,"efac9003-0ea8-4251-97d7-c1478ef51c29.0.3"),sQuery(id+"F6.wireOp",EDGE,"89777391-df2a-4d0b-bbf8-c0feeb0d1ef7.0.0"),sQuery(id+"F6.wireOp",EDGE,"89777391-df2a-4d0b-bbf8-c0feeb0d1ef7.0.2"),sQuery(id+"F6.wireOp",EDGE,"89777391-df2a-4d0b-bbf8-c0feeb0d1ef7.0.3"),sQuery(id+"F6.wireOp",EDGE,"5c4a4382-07f6-4214-aac6-78221b16e3d7.0.1"),sQuery(id+"F6.wireOp",EDGE,"5c4a4382-07f6-4214-aac6-78221b16e3d7.0.2"),sQuery(id+"F6.wireOp",EDGE,"5c4a4382-07f6-4214-aac6-78221b16e3d7.0.3"),sQuery(id+"F6.wireOp",EDGE,"f066974f-1994-491f-a93d-417e52911a5a.0.0"),sQuery(id+"F6.wireOp",EDGE,"f066974f-1994-491f-a93d-417e52911a5a.0.2"),sQuery(id+"F6.wireOp",EDGE,"f066974f-1994-491f-a93d-417e52911a5a.0.3"),sQuery(id+"F6.wireOp",EDGE,"95247560-69bb-48ff-a0da-1bb4b4d30057.0.1"),sQuery(id+"F6.wireOp",EDGE,"95247560-69bb-48ff-a0da-1bb4b4d30057.0.2"),sQuery(id+"F6.wireOp",EDGE,"95247560-69bb-48ff-a0da-1bb4b4d30057.0.3"),sQuery(id+"F6.wireOp",EDGE,"1d799f85-7818-430d-bbf1-0f564a028ddc.0.0"),sQuery(id+"F6.wireOp",EDGE,"1d799f85-7818-430d-bbf1-0f564a028ddc.0.2"),sQuery(id+"F6.wireOp",EDGE,"1d799f85-7818-430d-bbf1-0f564a028ddc.0.3"),sQuery(id+"F6.wireOp",EDGE,"6aa83139-d0d5-4dfc-9373-fda511bd29d7.trimOffspring"),sQuery(id+"F6.wireOp",EDGE,"1408c1dd-e7a2-410c-9066-205276191e3a.trimOffspring"),sQuery(id+"F6.wireOp",EDGE,"e31db4b1-2812-45a9-86ec-e541b6eb03b3.trimOffspring"),sQuery(id+"F6.wireOp",EDGE,"726fdc42-c52d-414d-8529-3d57c62d2646.trimOffspring"),sQuery(id+"F6.wireOp",EDGE,"85645508-a54a-4e30-b284-8fd3e0c44a2d.trimOffspring"),sQuery(id+"F6.wireOp",EDGE,"f6c9b0fd-1728-47da-b042-307b3b696b93.trimOffspring"),sQuery(id+"F6.wireOp",EDGE,"70f4a275-a1fe-4adc-966b-bca2063eecaf.trimOffspring"),sQuery(id+"F6.wireOp",EDGE,"3e7ab608-056d-4084-b8cf-19f53ae0a1b8.trimOffspring")])],"isStart":true});
            var Q4;
            Q4=makeQuery(id+"F7.opExtrude","CAP_FACE",FACE,{"disambiguationData":[OSD([sQuery(id+"F6.wireOp",EDGE,"E5.0"),sQuery(id+"F6.wireOp",EDGE,"E5.1"),sQuery(id+"F6.wireOp",EDGE,"E5.2"),sQuery(id+"F6.wireOp",EDGE,"E5.3"),sQuery(id+"F6.wireOp",EDGE,"E5.4"),sQuery(id+"F6.wireOp",EDGE,"E5.8"),sQuery(id+"F6.wireOp",EDGE,"E5.9"),sQuery(id+"F6.wireOp",EDGE,"E5.10"),sQuery(id+"F6.wireOp",EDGE,"E5.12"),sQuery(id+"F6.wireOp",EDGE,"E5.15"),sQuery(id+"F6.wireOp",EDGE,"E5.16"),sQuery(id+"F6.wireOp",EDGE,"E5.17"),sQuery(id+"F6.wireOp",EDGE,"E6.1.1"),sQuery(id+"F6.wireOp",EDGE,"E6.1.2"),sQuery(id+"F6.wireOp",EDGE,"E6.1.5"),sQuery(id+"F6.wireOp",EDGE,"E6.1.7"),sQuery(id+"F6.wireOp",EDGE,"E6.1.10"),sQuery(id+"F6.wireOp",EDGE,"E6.1.12"),sQuery(id+"F6.wireOp",EDGE,"E6.1.13"),sQuery(id+"F6.wireOp",EDGE,"E6.1.14"),sQuery(id+"F6.wireOp",EDGE,"E6.1.16"),sQuery(id+"F6.wireOp",EDGE,"E6.1.17"),sQuery(id+"F6.wireOp",EDGE,"E6.1.18"),sQuery(id+"F6.wireOp",EDGE,"E6.1.19"),sQuery(id+"F6.wireOp",EDGE,"E7"),sQuery(id+"F6.wireOp",EDGE,"E8.trimOffspring"),sQuery(id+"F6.wireOp",EDGE,"E9.trimOffspring"),sQuery(id+"F6.wireOp",EDGE,"E10.trimOffspring"),sQuery(id+"F6.wireOp",EDGE,"E11.trimOffspring"),sQuery(id+"F6.wireOp",EDGE,"E12.trimOffspring"),sQuery(id+"F6.wireOp",EDGE,"E13.trimOffspring"),sQuery(id+"F6.wireOp",EDGE,"E14.trimOffspring")])],"isStart":false});
            var Q5;
            Q5=makeQuery(id+"F7.opExtrude","CAP_FACE",FACE,{"disambiguationData":[OSD([sQuery(id+"F6.wireOp",EDGE,"E5.0"),sQuery(id+"F6.wireOp",EDGE,"E5.1"),sQuery(id+"F6.wireOp",EDGE,"E5.2"),sQuery(id+"F6.wireOp",EDGE,"E5.3"),sQuery(id+"F6.wireOp",EDGE,"E5.4"),sQuery(id+"F6.wireOp",EDGE,"E5.8"),sQuery(id+"F6.wireOp",EDGE,"E5.9"),sQuery(id+"F6.wireOp",EDGE,"E5.10"),sQuery(id+"F6.wireOp",EDGE,"E5.12"),sQuery(id+"F6.wireOp",EDGE,"E5.15"),sQuery(id+"F6.wireOp",EDGE,"E5.16"),sQuery(id+"F6.wireOp",EDGE,"E5.17"),sQuery(id+"F6.wireOp",EDGE,"E6.1.1"),sQuery(id+"F6.wireOp",EDGE,"E6.1.2"),sQuery(id+"F6.wireOp",EDGE,"E6.1.5"),sQuery(id+"F6.wireOp",EDGE,"E6.1.7"),sQuery(id+"F6.wireOp",EDGE,"E6.1.10"),sQuery(id+"F6.wireOp",EDGE,"E6.1.12"),sQuery(id+"F6.wireOp",EDGE,"E6.1.13"),sQuery(id+"F6.wireOp",EDGE,"E6.1.14"),sQuery(id+"F6.wireOp",EDGE,"E6.1.16"),sQuery(id+"F6.wireOp",EDGE,"E6.1.17"),sQuery(id+"F6.wireOp",EDGE,"E6.1.18"),sQuery(id+"F6.wireOp",EDGE,"E6.1.19"),sQuery(id+"F6.wireOp",EDGE,"E7"),sQuery(id+"F6.wireOp",EDGE,"E8.trimOffspring"),sQuery(id+"F6.wireOp",EDGE,"E9.trimOffspring"),sQuery(id+"F6.wireOp",EDGE,"E10.trimOffspring"),sQuery(id+"F6.wireOp",EDGE,"E11.trimOffspring"),sQuery(id+"F6.wireOp",EDGE,"E12.trimOffspring"),sQuery(id+"F6.wireOp",EDGE,"E13.trimOffspring"),sQuery(id+"F6.wireOp",EDGE,"E14.trimOffspring")])],"isStart":true});
            fillet(context, id + "F9", {"entities" : qUnion([Q0, Q1, Q2, Q3, Q4, Q5]), "radius" : .5 * mm, "tangentPropagation" : true, "allowEdgeOverflow" : false});
        }
    });
